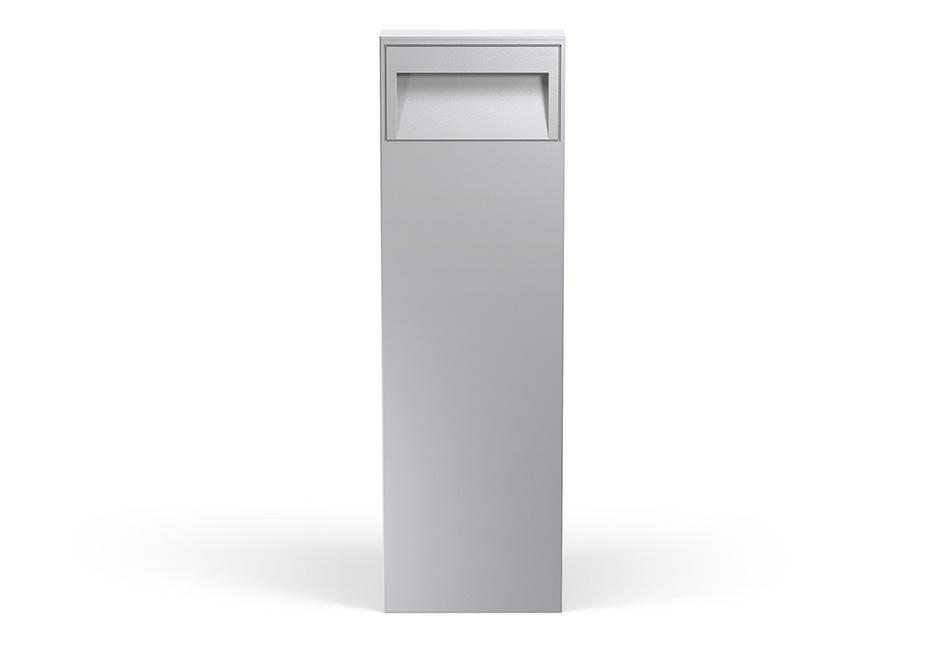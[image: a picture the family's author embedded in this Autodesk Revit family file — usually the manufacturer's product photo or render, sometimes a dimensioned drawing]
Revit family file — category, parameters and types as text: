
# Revit family: Platek_Team Bollard_1_Opening
name_source: partatom
category: Apparecchi per illuminazione
revit_build: Autodesk Revit 2017 (Build: 20160225_1515(x64)
units: mm (PartAtom-declared; Revit-internal decimal feet)

## family parameters
Basato su piano di lavoro = No
Condiviso = No
Punto di calcolo locali = No
Quota connettore circolare = Usa diametro
Sempre verticale = Sì
Sorgente d'illuminazione = Sì
Taglio con vuoti quando caricato = No
Tipo di parte = Normale

## types (2) — shared parameters
Aluminium = PLK_Light Source
Angolo inclinazione = 90.00°
Beam Angle = 0.00°
Body = PLK_Grey
CRI = >80
Cable Lenght = Max Ø 7mm
Carico apparente = 0 VA
Colour Temperature = 3000 K
Commenti sul tipo = Pedestrian areas, Urban zones, Paths, Roads
Descrizione = Outdoor Lighting, Floor/Ground Illumination
Diffuse Type = PMMA
Dimmable = Yes
Emetti da larghezza rettangolo = 23 mm  [stored 0.0754593 ft]
Emetti da lunghezza rettangolo = 230 mm  [stored 0.754593 ft]
Energy Efficiency Rating = A/A+/A++
Filtro dei colori = 16777215
Frequency = 50/60 Hz
IK Rating = IK 08
IP Rating = IP66
Insulation Class = 2
LED Protection = Surge protection included
Lampada = LED
Light Source = PLK_Light Source
Luminaire Luminous Flux = 894 lm
Luminaire Luminous Intensity = 725 cd
Luminaire Wattage = 17 W
Modello = TEAM BOLLARD
Mounting Type = Ground
Nota chiave = Other Led colors available on request
PLATEK FInishes = Painted Aluminium Avalaible in Anthracite/Black/White/Corten/Bronze
Power Supply Unit = Included
Product Documentation Link = http://www.platek.eu
Product Page URL = http://www.platek.eu
Produttore = PLATEK SRL
Rendi la forma visibile nel rendering = No
Supply Voltage = 230 V
Supply Voltage Max = 240 V
Supply Voltage Min = 220 V
URL = www.platek.eu
Variazione temperatura colore lampada con luminosità attenuata = <Nessuno>

## per-type parameters (varying)
| type | Codice assieme | File diagramma fotometrico | Height | Height 434_734 | Immagine tipo | Manufacturer Comment | PLATEK Article Code | Product Dimension |
| 3440419_17W_LED_3000K_H900mm | 3440419.06(Grey); 3440419.08(Anthracite); 3440419.01(Black); 3440419.02(White); 3440419.07(Corten); 3440419.09(Bronze) | 3440419.IES | 734 mm  [stored 2.40814 ft] | No | Team_paletto_900_2.jpg | Weight 7,00 Kg | 3440419 | L280mm x L102mm x H900mm |
| 3440619_17W_LED_3000K_H600mm | 3440619.06(Grey); 3440619.08(Anthracite); 3440619.01(Black); 3440619.02(White); 3440619.07(Corten); 3440619.09(Bronze) | 3440619.IES | 434 mm  [stored 1.42388 ft] | Sì | Team_paletto_600_2.jpg | Weight 4,50 Kg | 3440619 | L280mm x L102mm x H600mm |

note: [stored X ft] marks values corroborated as IEEE doubles in the binary element streams (Revit-internal decimal feet)
